# Revit family: 503_48bd82d0c57f4e5797a4f64ef84567
name_source: partatom
category: Lighting Devices
revit_build: Autodesk Revit 2018 (Build: 20170223_1515(x64)
units: mm (PartAtom-declared; Revit-internal decimal feet)

## family parameters
Cut with Voids When Loaded = No
Host = Face
Maintain Annotation Orientation = Yes
Part Type = Switch
Room Calculation Point = No
Round Connector Dimension = Use Diameter
Shared = No

## types (1)
- 111410
    DR = 10 mm  [stored 0.0328084 ft]
    DR1 = 12 mm  [stored 0.0393701 ft]
    Default Elevation = 0 mm  [stored 0 ft]
    Description = Pressure guard kitchen
    H2 = 37 mm
    KR = 3 mm  [stored 0.00984252 ft]
    L2 = 37 mm
    L2D = 0 mm  [stored 0 ft]
    MC Active Power = 1 W
    MC CosPhi = 0.95
    MC Number of Poles = 3
    MC Product Code = 111410
    MC Voltage = 0 V
    Manufacturer = Flexit
    SketchPlaneIDs = 10482;153b746f-b00a-47b6-946a-48530699bbd5-000028f2
    W1 = 7 mm  [stored 0.0229659 ft]
    W2 = 41 mm
    W2D = 0 mm  [stored 0 ft]
    XK = 8 mm  [stored 0.0262467 ft]
    XK__ve = -8 mm  [stored -0.0262467 ft]
    magiPartTypeId = 503
    magiProductFamilyId = 48bd82d0c57f4e5797a4f64ef84567
    magiProductId = 36a399394b3f494da59ba1b8c1914d

note: [stored X ft] marks values corroborated as IEEE doubles in the binary element streams (Revit-internal decimal feet)

## geometry (parser evidence)
native form markers: Sweep x2
no freeform markers — native parametric forms only
